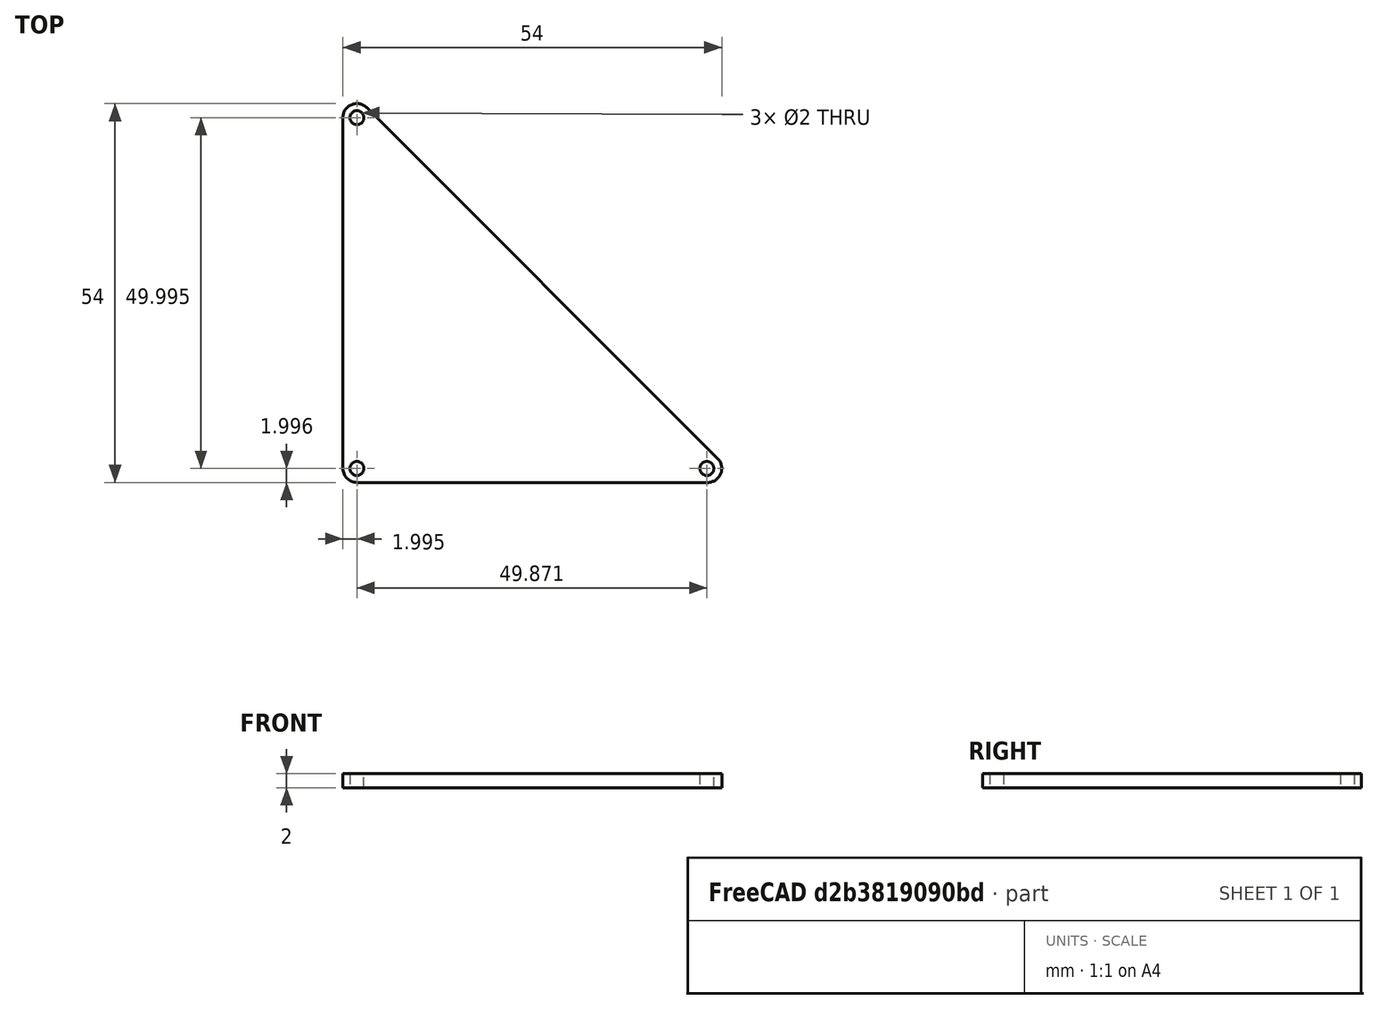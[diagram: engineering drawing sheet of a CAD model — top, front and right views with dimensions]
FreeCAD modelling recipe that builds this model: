
FCSTD DOCUMENT  (FreeCAD 0.16R6698 (Git))
Label: triangle maintien
License: All rights reserved
LicenseURL: http://en.wikipedia.org/wiki/All_rights_reserved
objects: Sketcher::SketchObject×1, PartDesign::Pad×1
note: 3 computed .brp shape members not serialized (recipe doc carries the construction recipe); baked Part::Feature solids carry a one-line shape summary decoded from their .brp

FEATURE [Sketcher::SketchObject] Sketch
  sketch-geometry (9):
    g0: LineSegment StartX=-23.8245 StartY=56.9861 StartZ=0 EndX=-23.8245 EndY=6.98611 EndZ=0
    g1: LineSegment StartX=-21.8245 StartY=4.98611 StartZ=0 EndX=28.1755 EndY=4.98611 EndZ=0
    g2: LineSegment StartX=29.5897 StartY=8.40033 StartZ=0 EndX=-20.4103 EndY=58.4003 EndZ=0
    g3: ArcOfCircle CenterX=-21.8245 CenterY=56.9861 CenterZ=0 NormalX=0 NormalY=0 NormalZ=1 Radius=2 StartAngle=0.785398 EndAngle=3.14159
    g4: ArcOfCircle CenterX=28.1755 CenterY=6.98611 CenterZ=0 NormalX=0 NormalY=0 NormalZ=1 Radius=2 StartAngle=4.71239 EndAngle=7.06858
    g5: ArcOfCircle CenterX=-21.8245 CenterY=6.98611 CenterZ=0 NormalX=0 NormalY=0 NormalZ=1 Radius=2 StartAngle=3.14159 EndAngle=4.71239
    g6: Circle CenterX=-21.8245 CenterY=56.9807 CenterZ=0 NormalX=0 NormalY=0 NormalZ=1 Radius=1
    g7: Circle CenterX=-21.8245 CenterY=6.98611 CenterZ=0 NormalX=0 NormalY=0 NormalZ=1 Radius=1
    g8: Circle CenterX=28.0468 CenterY=6.98611 CenterZ=0 NormalX=0 NormalY=0 NormalZ=1 Radius=1
  constraints (19):
    c: Vertical(g0)
    c: Horizontal(g1)
    c: Tangent(g2,g3) = -1.5708
    c: Tangent(g0,g3) = -1.5708
    c: Tangent(g2,g4) = -1.5708
    c: Tangent(g1,g4) = -1.5708
    c: Tangent(g0,g5) = -1.5708
    c: Tangent(g1,g5) = -1.5708
    c: Radius(g3) = 2
    c: Equal(g3,g4)
    c: Radius(g5) = 2
    c: DistanceY(g0,g0) = 50
    c: DistanceX(g1,g1) = 50
    c: Radius(g8) = 1
    c: Equal(g8,g7)
    c: Equal(g8,g6)
    c: Coincident(g5,g7)
    c: DistanceY(g8,g5) = 0
    c: DistanceX(g6,g5) = 0
FEATURE [PartDesign::Pad] Pad
  Length = 2
  Length2 = 100
  Sketch = -> Sketch
  Type = 0
